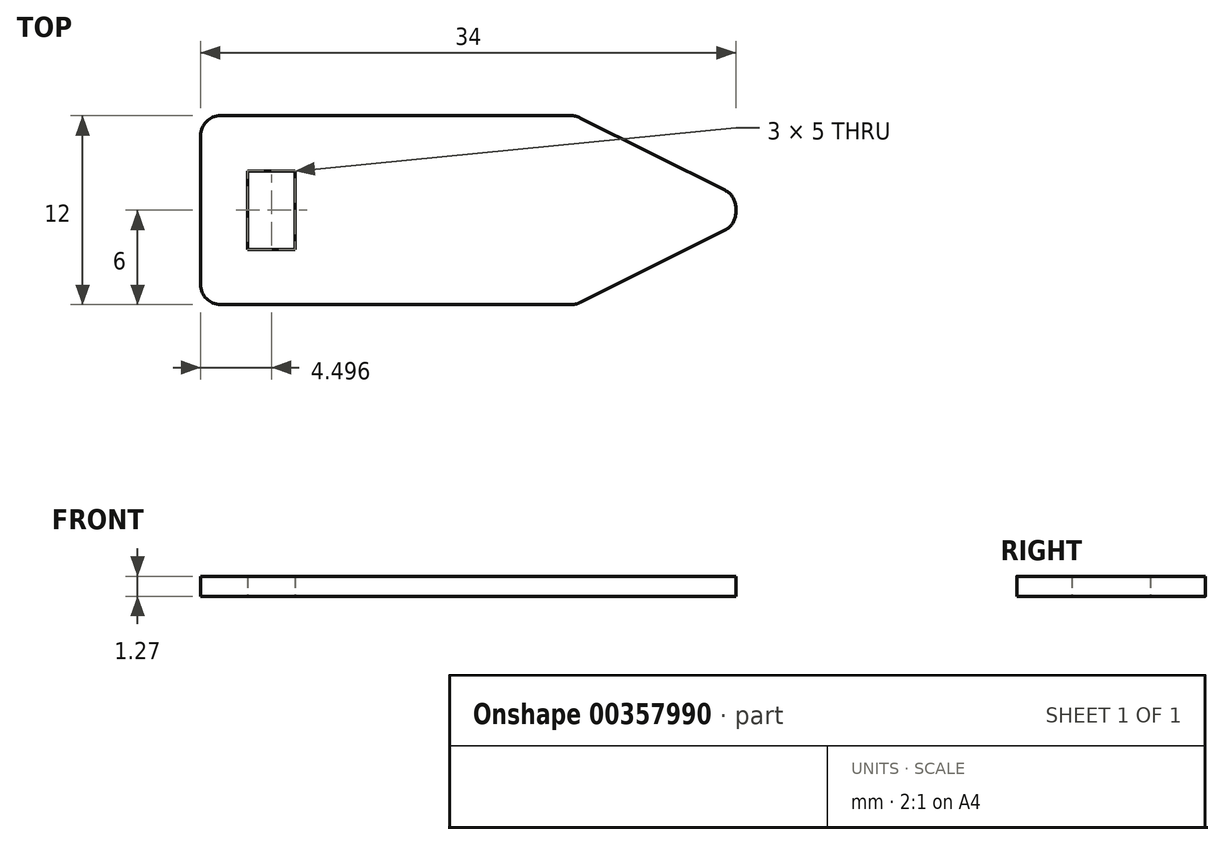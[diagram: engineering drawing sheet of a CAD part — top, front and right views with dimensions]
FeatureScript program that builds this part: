
annotation { "Feature Type Name" : "Feature", "Feature Type Description" : "" }
export const myFeature = defineFeature(function(context is Context, id is Id, definition is map)
    precondition{}
    {
        {
            var Q0;
            Q0=qCreatedBy(makeId("Top.planeOp"),FACE);
            var sketch = newSketch(context, id + "F0", { "sketchPlane" : qUnion([Q0])});
            skLineSegment(sketch, "E0.bottom", {"start": v(-45.13, -30.26) * mm, "end": v(-11.13, -30.26) * mm});
            skLineSegment(sketch, "E0.top", {"start": v(-45.13, -42.26) * mm, "end": v(-11.13, -42.26) * mm});
            skLineSegment(sketch, "E0.left", {"start": v(-45.13, -30.26) * mm, "end": v(-45.13, -42.26) * mm});
            skLineSegment(sketch, "E0.right", {"start": v(-11.13, -30.26) * mm, "end": v(-11.13, -42.26) * mm});
            skLineSegment(sketch, "E1", {"start": v(-42.13, -30.26) * mm, "end": v(-42.13, -42.26) * mm});
            skLineSegment(sketch, "E2", {"start": v(-39.13, -30.26) * mm, "end": v(-39.13, -42.26) * mm});
            skLineSegment(sketch, "E3", {"start": v(-36.13, -30.26) * mm, "end": v(-36.13, -42.26) * mm});
            skLineSegment(sketch, "E4.bottom", {"start": v(-42.13, -33.76) * mm, "end": v(-39.13, -33.76) * mm});
            skLineSegment(sketch, "E4.top", {"start": v(-42.13, -38.76) * mm, "end": v(-39.13, -38.76) * mm});
            skLineSegment(sketch, "E4.left", {"start": v(-42.13, -33.76) * mm, "end": v(-42.13, -38.76) * mm});
            skLineSegment(sketch, "E4.right", {"start": v(-39.13, -33.76) * mm, "end": v(-39.13, -38.76) * mm});
            skSolve(sketch);
        }
        {
            var Q0;
            {var subQ0=sQuery(id+"F0.wireOp",EDGE,"E0.left");Q0=makeQuery(id+"F0.imprint","IMPRINT",FACE,{"disambiguationData":[TD([[makeQuery(id+"F0.imprint","IMPRINT",EDGE,{"derivedFrom":subQ0}),1.0]])]});}
            var Q1;
            {var subQ5=sQuery(id+"F0.wireOp",EDGE,"E4.bottom");Q1=makeQuery(id+"F0.imprint","IMPRINT",FACE,{"disambiguationData":[TD([[makeQuery(id+"F0.imprint","IMPRINT",EDGE,{"derivedFrom":subQ5}),1.0]])]});}
            var Q2;
            {var subQ5=sQuery(id+"F0.wireOp",EDGE,"E4.top");Q2=makeQuery(id+"F0.imprint","IMPRINT",FACE,{"disambiguationData":[TD([[makeQuery(id+"F0.imprint","IMPRINT",EDGE,{"derivedFrom":subQ5}),-1.0]])]});}
            var Q3;
            {var subQ6=sQuery(id+"F0.wireOp",EDGE,"E3");Q3=makeQuery(id+"F0.imprint","IMPRINT",FACE,{"disambiguationData":[TD([[makeQuery(id+"F0.imprint","IMPRINT",EDGE,{"derivedFrom":subQ6}),-1.0]])]});}
            var Q4;
            {var subQ0=sQuery(id+"F0.wireOp",EDGE,"E0.right");Q4=makeQuery(id+"F0.imprint","IMPRINT",FACE,{"disambiguationData":[TD([[makeQuery(id+"F0.imprint","IMPRINT",EDGE,{"derivedFrom":subQ0}),-1.0]])]});}
            extrude(context, id + "F1", {"entities" : qUnion([Q0, Q1, Q2, Q3, Q4]), "depth" : 1.27 * mm});
        }
        {
            var Q0;
            Q0=makeQuery(id+"F1.opExtrude","SWEPT_EDGE",EDGE,{"disambiguationData":[OSD([sQuery(id+"F0.wireOp",EDGE,"E0.bottom"),sQuery(id+"F0.wireOp",EDGE,"E0.right")])]});
            var Q1;
            Q1=makeQuery(id+"F1.opExtrude","SWEPT_EDGE",EDGE,{"disambiguationData":[OSD([sQuery(id+"F0.wireOp",EDGE,"E0.top"),sQuery(id+"F0.wireOp",EDGE,"E0.right")])]});
            chamfer(context, id + "F2", {"entities" : qUnion([Q0, Q1]), "chamferType" : ChamferType.TWO_OFFSETS, "width1" : 10.16 * mm, "oppositeDirection" : false, "width2" : 5.08 * mm, "tangentPropagation" : true});
        }
        {
            var Q0;
            {var subQ0=sQuery(id+"F0.wireOp",EDGE,"E0.bottom");Q0=makeQuery(id+"F2.opChamfer","BLEND_EDGE",EDGE,{"blendedFrom":[makeQuery(id+"F1.opExtrude","SWEPT_EDGE",EDGE,{"disambiguationData":[OSD([subQ0,sQuery(id+"F0.wireOp",EDGE,"E0.right")])]}),makeQuery(id+"F1.opExtrude","SWEPT_FACE",FACE,{"disambiguationData":[OSD([subQ0])]})],"blendedInto":[makeQuery(id+"F1.opExtrude","SWEPT_FACE",FACE,{"disambiguationData":[OSD([subQ0])]})]});}
            var Q1;
            {var subQ0=sQuery(id+"F0.wireOp",EDGE,"E0.right");Q1=makeQuery(id+"F2.opChamfer","BLEND_EDGE",EDGE,{"blendedFrom":[makeQuery(id+"F1.opExtrude","SWEPT_EDGE",EDGE,{"disambiguationData":[OSD([sQuery(id+"F0.wireOp",EDGE,"E0.bottom"),subQ0])]}),makeQuery(id+"F1.opExtrude","SWEPT_FACE",FACE,{"disambiguationData":[OSD([subQ0])]})],"blendedInto":[makeQuery(id+"F1.opExtrude","SWEPT_FACE",FACE,{"disambiguationData":[OSD([subQ0])]})]});}
            var Q2;
            {var subQ0=sQuery(id+"F0.wireOp",EDGE,"E0.right");Q2=makeQuery(id+"F2.opChamfer","BLEND_EDGE",EDGE,{"blendedFrom":[makeQuery(id+"F1.opExtrude","SWEPT_EDGE",EDGE,{"disambiguationData":[OSD([sQuery(id+"F0.wireOp",EDGE,"E0.top"),subQ0])]}),makeQuery(id+"F1.opExtrude","SWEPT_FACE",FACE,{"disambiguationData":[OSD([subQ0])]})],"blendedInto":[makeQuery(id+"F1.opExtrude","SWEPT_FACE",FACE,{"disambiguationData":[OSD([subQ0])]})]});}
            var Q3;
            {var subQ0=sQuery(id+"F0.wireOp",EDGE,"E0.top");Q3=makeQuery(id+"F2.opChamfer","BLEND_EDGE",EDGE,{"blendedFrom":[makeQuery(id+"F1.opExtrude","SWEPT_EDGE",EDGE,{"disambiguationData":[OSD([subQ0,sQuery(id+"F0.wireOp",EDGE,"E0.right")])]}),makeQuery(id+"F1.opExtrude","SWEPT_FACE",FACE,{"disambiguationData":[OSD([subQ0])]})],"blendedInto":[makeQuery(id+"F1.opExtrude","SWEPT_FACE",FACE,{"disambiguationData":[OSD([subQ0])]})]});}
            fillet(context, id + "F3", {"entities" : qUnion([Q0, Q1, Q2, Q3]), "radius" : 1.27 * mm, "tangentPropagation" : true, "allowEdgeOverflow" : false});
        }
        {
            var Q0;
            Q0=makeQuery(id+"F1.opExtrude","SWEPT_EDGE",EDGE,{"disambiguationData":[OSD([sQuery(id+"F0.wireOp",EDGE,"E0.top"),sQuery(id+"F0.wireOp",EDGE,"E0.left")])]});
            var Q1;
            Q1=makeQuery(id+"F1.opExtrude","SWEPT_EDGE",EDGE,{"disambiguationData":[OSD([sQuery(id+"F0.wireOp",EDGE,"E0.bottom"),sQuery(id+"F0.wireOp",EDGE,"E0.left")])]});
            fillet(context, id + "F4", {"entities" : qUnion([Q0, Q1]), "radius" : 1.27 * mm, "tangentPropagation" : true, "allowEdgeOverflow" : false});
        }
    });
